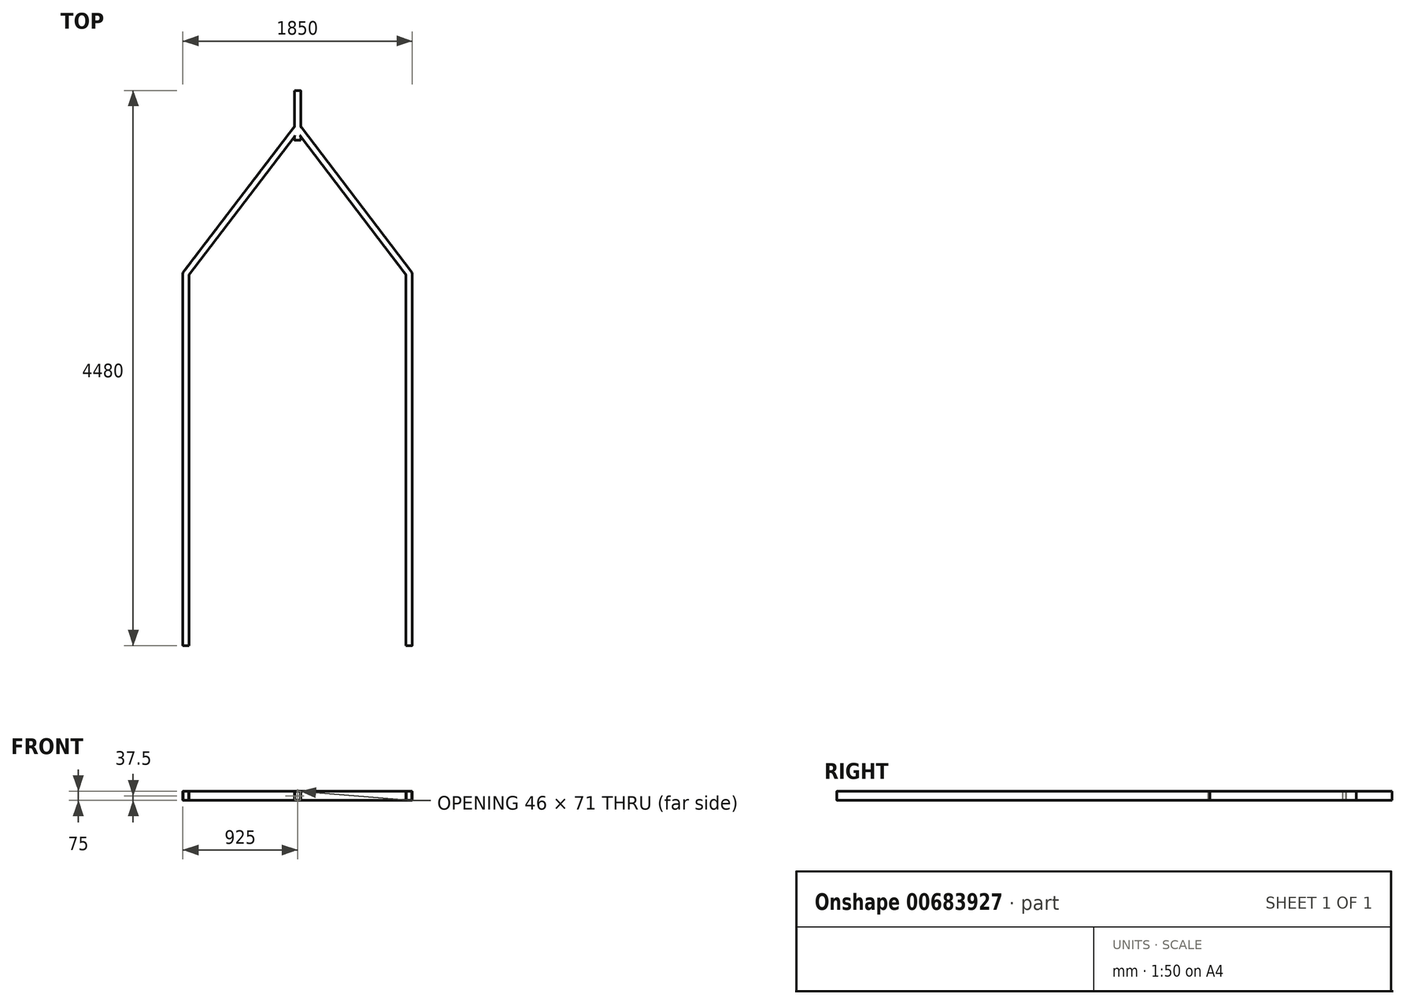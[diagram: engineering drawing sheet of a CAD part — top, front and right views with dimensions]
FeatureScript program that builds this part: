
annotation { "Feature Type Name" : "Feature", "Feature Type Description" : "" }
export const myFeature = defineFeature(function(context is Context, id is Id, definition is map)
    precondition{}
    {
        {
            var Q0;
            Q0=qCreatedBy(makeId("Top.planeOp"),FACE);
            var sketch = newSketch(context, id + "F0", { "sketchPlane" : qUnion([Q0])});
            skLineSegment(sketch, "E0", {"start": v(0, 0) * mm, "end": v(0, -300) * mm});
            skLineSegment(sketch, "E1", {"start": v(0, -300) * mm, "end": v(-900, -1480) * mm});
            skLineSegment(sketch, "E2", {"start": v(-900, -1480) * mm, "end": v(-900, -4480) * mm});
            skLineSegment(sketch, "E3", {"start": v(0, -300) * mm, "end": v(0, -400) * mm});
            skSolve(sketch);
        }
        {
            var Q0;
            Q0=qCreatedBy(makeId("Front.planeOp"),FACE);
            var sketch = newSketch(context, id + "F1", { "sketchPlane" : qUnion([Q0])});
            skLineSegment(sketch, "E4.bottom", {"start": v(25, 37.5) * mm, "end": v(-25, 37.5) * mm});
            skLineSegment(sketch, "E4.top", {"start": v(25, -37.5) * mm, "end": v(-25, -37.5) * mm});
            skLineSegment(sketch, "E4.left", {"start": v(25, 37.5) * mm, "end": v(25, -37.5) * mm});
            skLineSegment(sketch, "E4.right", {"start": v(-25, 37.5) * mm, "end": v(-25, -37.5) * mm});
            skSolve(sketch);
        }
        {
            var Q0;
            Q0=makeQuery(id+"F1.imprint","IMPRINT",FACE,{"disambiguationData":[TD([[makeQuery(id+"F1.imprint","IMPRINT",EDGE,{"derivedFrom":sQuery(id+"F1.wireOp",EDGE,"E4.bottom")}),1.0]])]});
            var Q1;
            Q1=sQuery(id+"F0.wireOp",EDGE,"E0");
            var Q2;
            Q2=sQuery(id+"F0.wireOp",EDGE,"E1");
            var Q3;
            Q3=sQuery(id+"F0.wireOp",EDGE,"E2");
            sweep(context, id + "F2", {"profiles" : qUnion([Q0]), "path" : qUnion([Q1, Q2, Q3])});
        }
        {
            var Q0;
            Q0=makeQuery(id+"F2.opSweep","CAP_FACE",FACE,{"disambiguationData":[OSD([sQuery(id+"F0.wireOp",VERTEX,"E0.start"),sQuery(id+"F1.wireOp",EDGE,"E4.bottom"),sQuery(id+"F1.wireOp",EDGE,"E4.top"),sQuery(id+"F1.wireOp",EDGE,"E4.left"),sQuery(id+"F1.wireOp",EDGE,"E4.right")])],"isStart":true});
            extrude(context, id + "F3", {"entities" : qUnion([Q0]), "operationType" : NewBodyOperationType.ADD, "oppositeDirection" : true, "depth" : 400 * mm, "offsetDistance" : 25 * mm});
        }
        {
            var Q0;
            Q0=makeQuery(id+"F2.opSweep","SWEPT_EDGE",EDGE,{"disambiguationData":[OSD([sQuery(id+"F0.wireOp",EDGE,"E2"),sQuery(id+"F1.wireOp",EDGE,"E4.top"),sQuery(id+"F1.wireOp",EDGE,"E4.left")])]});
            var Q1;
            Q1=makeQuery(id+"F2.opSweep","SWEPT_EDGE",EDGE,{"disambiguationData":[OSD([sQuery(id+"F0.wireOp",EDGE,"E2"),sQuery(id+"F1.wireOp",EDGE,"E4.bottom"),sQuery(id+"F1.wireOp",EDGE,"E4.left")])]});
            var Q2;
            Q2=makeQuery(id+"F2.opSweep","SWEPT_EDGE",EDGE,{"disambiguationData":[OSD([sQuery(id+"F0.wireOp",EDGE,"E2"),sQuery(id+"F1.wireOp",EDGE,"E4.bottom"),sQuery(id+"F1.wireOp",EDGE,"E4.right")])]});
            var Q3;
            Q3=makeQuery(id+"F2.opSweep","SWEPT_EDGE",EDGE,{"disambiguationData":[OSD([sQuery(id+"F0.wireOp",EDGE,"E2"),sQuery(id+"F1.wireOp",EDGE,"E4.top"),sQuery(id+"F1.wireOp",EDGE,"E4.right")])]});
            var Q4;
            Q4=makeQuery(id+"F2.opSweep","SWEPT_EDGE",EDGE,{"disambiguationData":[OSD([sQuery(id+"F0.wireOp",EDGE,"E1"),sQuery(id+"F1.wireOp",EDGE,"E4.top"),sQuery(id+"F1.wireOp",EDGE,"E4.left")])]});
            var Q5;
            Q5=makeQuery(id+"F2.opSweep","SWEPT_EDGE",EDGE,{"disambiguationData":[OSD([sQuery(id+"F0.wireOp",EDGE,"E1"),sQuery(id+"F1.wireOp",EDGE,"E4.bottom"),sQuery(id+"F1.wireOp",EDGE,"E4.left")])]});
            var Q6;
            Q6=makeQuery(id+"F2.opSweep","SWEPT_EDGE",EDGE,{"disambiguationData":[OSD([sQuery(id+"F0.wireOp",EDGE,"E1"),sQuery(id+"F1.wireOp",EDGE,"E4.top"),sQuery(id+"F1.wireOp",EDGE,"E4.right")])]});
            var Q7;
            Q7=makeQuery(id+"F2.opSweep","SWEPT_EDGE",EDGE,{"disambiguationData":[OSD([sQuery(id+"F0.wireOp",EDGE,"E1"),sQuery(id+"F1.wireOp",EDGE,"E4.bottom"),sQuery(id+"F1.wireOp",EDGE,"E4.right")])]});
            var Q8;
            {var subQ0=sQuery(id+"F1.wireOp",EDGE,"E4.bottom");var subQ3=sQuery(id+"F1.wireOp",EDGE,"E4.left");var subQ4=sQuery(id+"F0.wireOp",EDGE,"E0");var subQ5=sQuery(id+"F1.wireOp",EDGE,"E4.right");Q8=makeQuery(id+"FiZZuQ4wI3bgejE_1.boolean.opBoolean","SPLIT",EDGE,{"disambiguationData":[TD([makeQuery(id+"FiZZuQ4wI3bgejE_1.opPattern","COPY",FACE,{"derivedFrom":makeQuery(id+"F2.opSweep","SWEPT_FACE",FACE,{"disambiguationData":[OSD([sQuery(id+"F0.wireOp",EDGE,"E1"),subQ5])]}),"instanceName":"1"})])],"derivedFrom":makeQuery(id+"F3.boolean.opBoolean","MERGE",EDGE,{"derivedFrom":[makeQuery(id+"F2.opSweep","SWEPT_EDGE",EDGE,{"disambiguationData":[OSD([subQ4,subQ0,subQ3])]}),makeQuery(id+"F3.opExtrude","SWEPT_EDGE",EDGE,{"disambiguationData":[OSD([subQ4,subQ0,subQ3])]})]})});}
            var Q9;
            Q9=makeQuery(id+"F2.opSweep","SWEPT_EDGE",EDGE,{"disambiguationData":[OSD([sQuery(id+"F0.wireOp",EDGE,"E0"),sQuery(id+"F1.wireOp",EDGE,"E4.bottom"),sQuery(id+"F1.wireOp",EDGE,"E4.right")])]});
            var Q10;
            Q10=makeQuery(id+"F2.opSweep","SWEPT_EDGE",EDGE,{"disambiguationData":[OSD([sQuery(id+"F0.wireOp",EDGE,"E0"),sQuery(id+"F1.wireOp",EDGE,"E4.top"),sQuery(id+"F1.wireOp",EDGE,"E4.right")])]});
            var Q11;
            {var subQ0=sQuery(id+"F1.wireOp",EDGE,"E4.left");var subQ1=sQuery(id+"F1.wireOp",EDGE,"E4.top");var subQ2=sQuery(id+"F0.wireOp",EDGE,"E0");Q11=makeQuery(id+"F3.boolean.opBoolean","MERGE",EDGE,{"derivedFrom":[makeQuery(id+"F2.opSweep","SWEPT_EDGE",EDGE,{"disambiguationData":[OSD([subQ2,subQ1,subQ0])]}),makeQuery(id+"F3.opExtrude","SWEPT_EDGE",EDGE,{"disambiguationData":[OSD([subQ2,subQ1,subQ0])]})]});}
            var Q12;
            Q12=makeQuery(id+"F3.opExtrude","SWEPT_EDGE",EDGE,{"disambiguationData":[OSD([sQuery(id+"F0.wireOp",EDGE,"E0"),sQuery(id+"F1.wireOp",EDGE,"E4.bottom"),sQuery(id+"F1.wireOp",EDGE,"E4.right")])]});
            var Q13;
            Q13=makeQuery(id+"F3.opExtrude","SWEPT_EDGE",EDGE,{"disambiguationData":[OSD([sQuery(id+"F0.wireOp",EDGE,"E0"),sQuery(id+"F1.wireOp",EDGE,"E4.top"),sQuery(id+"F1.wireOp",EDGE,"E4.right")])]});
            fillet(context, id + "F4", {"entities" : qUnion([Q0, Q1, Q2, Q3, Q4, Q5, Q6, Q7, Q8, Q9, Q10, Q11, Q12, Q13]), "radius" : 4 * mm, "tangentPropagation" : true, "allowEdgeOverflow" : false});
        }
        {
            var Q0;
            Q0=makeQuery(id+"F2.opSweep","SWEPT_BODY",BODY,{"disambiguationData":[OSD([sQuery(id+"F0.wireOp",EDGE,"E2"),sQuery(id+"F1.wireOp",EDGE,"E4.bottom"),sQuery(id+"F1.wireOp",EDGE,"E4.top"),sQuery(id+"F1.wireOp",EDGE,"E4.left"),sQuery(id+"F1.wireOp",EDGE,"E4.right")])]});
            var Q1;
            Q1=qCreatedBy(makeId("Right.planeOp"),FACE);
            mirror(context, id + "F5", {"operationType" : NewBodyOperationType.ADD, "entities" : qUnion([Q0]), "mirrorPlane" : qUnion([Q1])});
        }
        {
            var Q0;
            Q0=makeQuery(id+"F2.opSweep","CAP_FACE",FACE,{"disambiguationData":[OSD([sQuery(id+"F0.wireOp",VERTEX,"E2.end"),sQuery(id+"F1.wireOp",EDGE,"E4.bottom"),sQuery(id+"F1.wireOp",EDGE,"E4.top"),sQuery(id+"F1.wireOp",EDGE,"E4.left"),sQuery(id+"F1.wireOp",EDGE,"E4.right")])],"isStart":false});
            var Q1;
            Q1=makeQuery(id+"F5.opPattern","COPY",FACE,{"derivedFrom":makeQuery(id+"F2.opSweep","CAP_FACE",FACE,{"disambiguationData":[OSD([sQuery(id+"F0.wireOp",VERTEX,"E2.end"),sQuery(id+"F1.wireOp",EDGE,"E4.bottom"),sQuery(id+"F1.wireOp",EDGE,"E4.top"),sQuery(id+"F1.wireOp",EDGE,"E4.left"),sQuery(id+"F1.wireOp",EDGE,"E4.right")])],"isStart":false}),"instanceName":"1"});
            var Q2;
            Q2=makeQuery(id+"F3.opExtrude","CAP_FACE",FACE,{"disambiguationData":[OSD([sQuery(id+"F0.wireOp",VERTEX,"E0.start"),sQuery(id+"F1.wireOp",EDGE,"E4.bottom"),sQuery(id+"F1.wireOp",EDGE,"E4.top"),sQuery(id+"F1.wireOp",EDGE,"E4.left"),sQuery(id+"F1.wireOp",EDGE,"E4.right")])],"isStart":false});
            var Q3;
            Q3=makeQuery(id+"F2.opSweep","CAP_FACE",FACE,{"disambiguationData":[OSD([sQuery(id+"F0.wireOp",VERTEX,"E0.start"),sQuery(id+"F1.wireOp",EDGE,"E4.bottom"),sQuery(id+"F1.wireOp",EDGE,"E4.top"),sQuery(id+"F1.wireOp",EDGE,"E4.left"),sQuery(id+"F1.wireOp",EDGE,"E4.right")])],"isStart":true});
            shell(context, id + "F6", {"entities" : qUnion([Q0, Q1, Q2, Q3]), "thickness" : 2 * mm});
        }
    });
